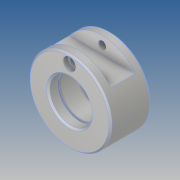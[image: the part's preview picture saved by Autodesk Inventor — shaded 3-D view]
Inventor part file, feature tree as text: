
AUTODESK INVENTOR PART (.ipt)
format: ipt  version: 2018.2 (Build 222227000, 227)  size: 184,320 bytes
history: native  units: mm
features: sketch x4, other x2, chamfer x2, extrude x1, hole x1, mirror x1
ambient origin geometry x8: Origin, YZ Plane, XZ Plane, XY Plane, X Axis, Y Axis, Z Axis, Center Point
bodies: Body1 (feature_tree)
feature tree (11):
  other  "Grundkörper"
  extrude  "Profil_Ausschnitt"  Depth=50.0mm
  hole  "DIN7984_M8_Boh"  [1 undecoded]
  mirror  "Spiegelung_DIN7984_M8_Boh"
  other  "DIN472-52x2-Nut"
  chamfer  "Fase_Allgemein"  Distance=30.0mm
  chamfer  "Fase2"  Distance=20.0mm
  sketch  "Skizze3"  dims[d8=100.0mm d9=50.0mm]
  sketch  "Skizze4"  dims[d10=52.0mm d11=22.2mm]
  sketch  "Skizze5"  dims[d13=45.0mm]
  sketch  "Skizze7"  dims[d16=90.0deg d17=30.0mm d18=20.0mm d19=10.0mm d20=0.0mm d21=9.0mm d22=6.0mm d23=15.0mm d24=5.4mm d25=90.0deg d26=8.0mm d27=20.594885mm d28=2.0mm d29=2.0mm d30=45.0deg d34=55.0mm d35=2.15mm d36=22.2mm d37=90.0deg d38=0.2mm d39=2.0mm d40=45.0deg]
note: 1 required parameter value undecoded (feature->parameter linkage not recoverable at this tier; creation-order binding heuristic only, values carry confidence <= 0.55)
